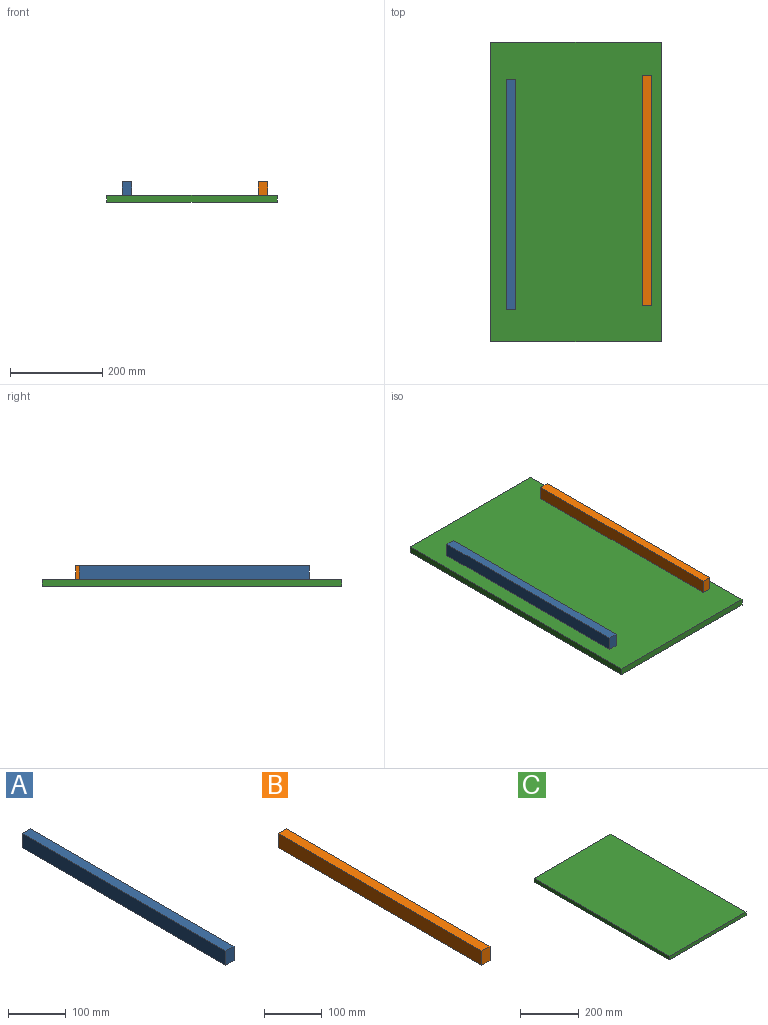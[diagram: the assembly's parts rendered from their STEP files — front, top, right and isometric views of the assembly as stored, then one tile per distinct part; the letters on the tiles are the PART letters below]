
ASSEMBLY  parts=3 mates=2
PART A: 6 faces, bbox 20x500x30 mm
  f0: plane 500x30mm, normal (1,0,0), area 15000mm2, adj f1,f3,f4,f5
  f1: plane 30x20mm, normal (0,1,0), area 600mm2, adj f0,f2,f4,f5
  f2: plane 500x30mm, normal (-1,0,0), area 15000mm2, adj f1,f3,f4,f5
  f3: plane 30x20mm, normal (0,-1,0), area 600mm2, adj f0,f2,f4,f5
  f4: plane 500x20mm, normal (0,0,1), area 10000mm2, adj f0,f1,f2,f3
  f5: plane 500x20mm, normal (0,0,-1), area 10000mm2, adj f0,f1,f2,f3
PART B: 6 faces, bbox 20x500x30 mm
  f0: plane 30x20mm, normal (0,1,0), area 600mm2, adj f1,f3,f4,f5
  f1: plane 500x30mm, normal (-1,0,0), area 15000mm2, adj f0,f2,f4,f5
  f2: plane 30x20mm, normal (0,-1,0), area 600mm2, adj f1,f3,f4,f5
  f3: plane 500x30mm, normal (1,0,0), area 15000mm2, adj f0,f2,f4,f5
  f4: plane 500x20mm, normal (0,0,1), area 10000mm2, adj f0,f1,f2,f3
  f5: plane 500x20mm, normal (0,0,-1), area 10000mm2, adj f0,f1,f2,f3
PART C: 6 faces, bbox 370x650x15 mm
  f0: plane 370x15mm, normal (0,-1,0), area 5550mm2, adj f1,f3,f4,f5
  f1: plane 650x15mm, normal (1,0,0), area 9750mm2, adj f0,f2,f4,f5
  f2: plane 370x15mm, normal (0,1,0), area 5550mm2, adj f1,f3,f4,f5
  f3: plane 650x15mm, normal (-1,0,0), area 9750mm2, adj f0,f2,f4,f5
  f4: plane 650x370mm, normal (0,0,1), area 240500mm2, adj f0,f1,f2,f3
  f5: plane 650x370mm, normal (0,0,-1), area 240500mm2, adj f0,f1,f2,f3
PLACE A t=(-304.35,134.7,349.88)mm
PLACE B t=(-337.1,141.89,349.88)mm
PLACE C t=(-327.15,139.31,334.88)mm
MATE planar C.f4 <-> B.f5  axis (0,0,1) through (-327.15,139.31,349.88)mm
MATE planar A.f5 <-> C.f4  axis (0,0,-1) through (-468.35,134.7,349.88)mm
